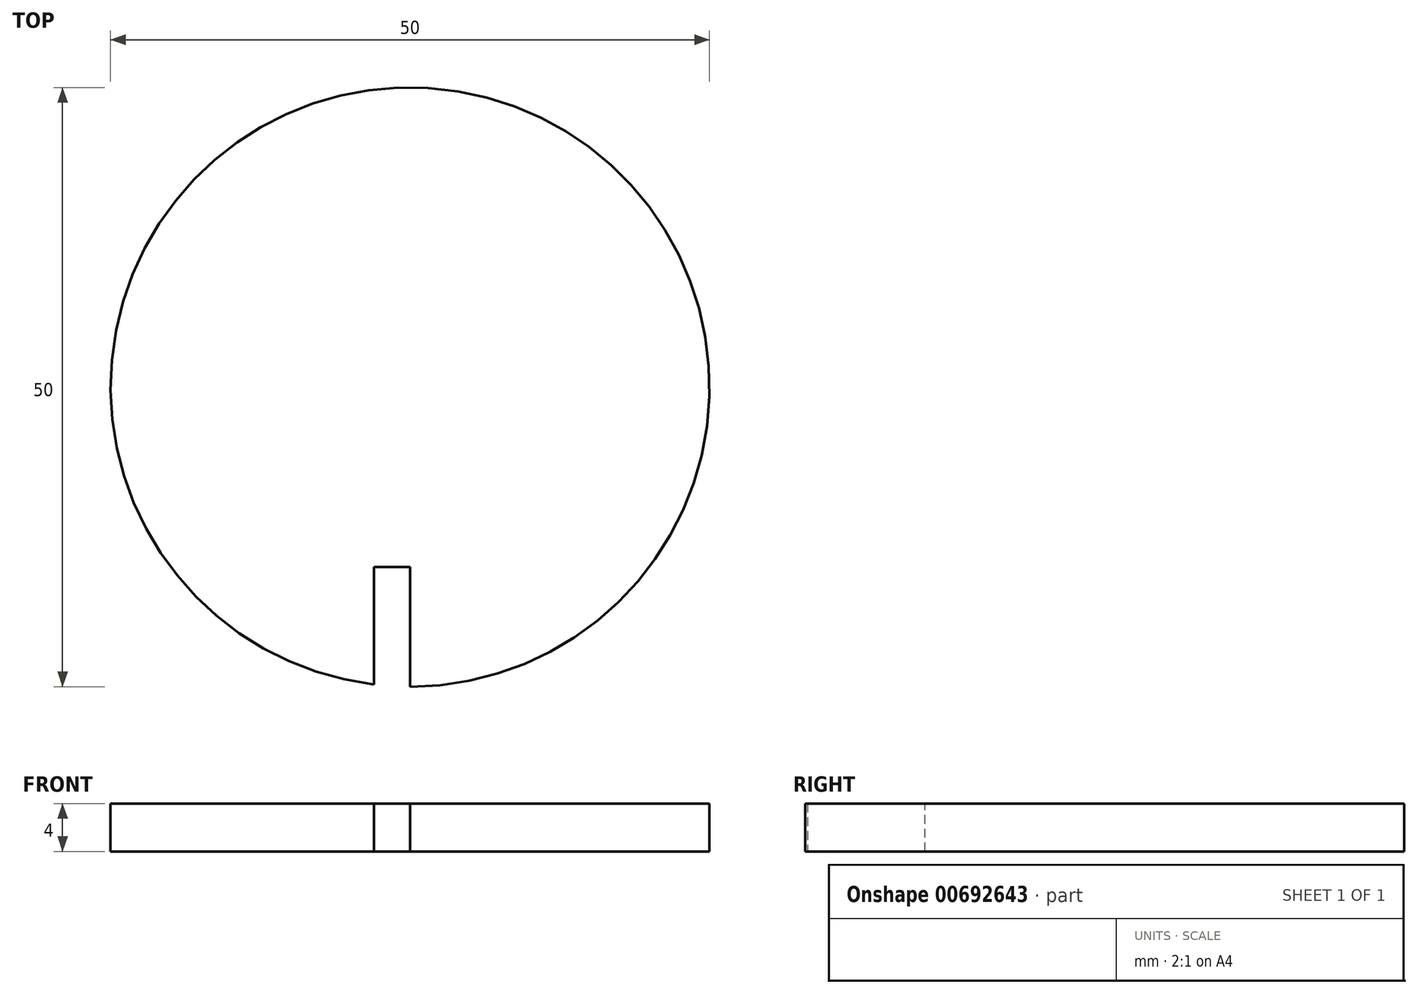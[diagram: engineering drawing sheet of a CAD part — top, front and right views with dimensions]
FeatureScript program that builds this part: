
annotation { "Feature Type Name" : "Feature", "Feature Type Description" : "" }
export const myFeature = defineFeature(function(context is Context, id is Id, definition is map)
    precondition{}
    {
        {
            var Q0;
            Q0=qCreatedBy(makeId("Top.planeOp"),FACE);
            var sketch = newSketch(context, id + "F0", { "sketchPlane" : qUnion([Q0])});
            skCircle(sketch, "E0", {"center": v(0, 0) * mm, "radius": 25 * mm});
            skSolve(sketch);
        }
        {
            var Q0;
            Q0 = qSketchRegion(id + "F0", true);
            extrude(context, id + "F1", {"entities" : qUnion([Q0]), "depth" : 4 * mm, "offsetDistance" : 25 * mm});
        }
        {
            var Q0;
            Q0=makeQuery(id+"F1.opExtrude","CAP_FACE",FACE,{"disambiguationData":[OSD([sQuery(id+"F0.wireOp",EDGE,"E0")])],"isStart":false});
            var sketch = newSketch(context, id + "F2", { "sketchPlane" : qUnion([Q0])});
            skLineSegment(sketch, "E1.bottom", {"start": v(0, -15) * mm, "end": v(-3, -15) * mm});
            skLineSegment(sketch, "E1.top", {"start": v(0, -25) * mm, "end": v(-3, -25) * mm});
            skLineSegment(sketch, "E1.left", {"start": v(0, -15) * mm, "end": v(0, -25) * mm});
            skLineSegment(sketch, "E1.right", {"start": v(-3, -15) * mm, "end": v(-3, -25) * mm});
            skSolve(sketch);
        }
        {
            var Q0;
            {var subQ0=sQuery(id+"F2.wireOp",EDGE,"E1.top");Q0=makeQuery(id+"F2.imprint","IMPRINT",FACE,{"disambiguationData":[TD([[makeQuery(id+"F2.imprint","IMPRINT",EDGE,{"derivedFrom":subQ0}),-1.0]])]});}
            var Q1;
            {var subQ0=sQuery(id+"F2.wireOp",EDGE,"E1.bottom");Q1=makeQuery(id+"F2.imprint","IMPRINT",FACE,{"disambiguationData":[TD([[makeQuery(id+"F2.imprint","IMPRINT",EDGE,{"derivedFrom":subQ0}),1.0]])]});}
            extrude(context, id + "F3", {"entities" : qUnion([Q0, Q1]), "operationType" : NewBodyOperationType.REMOVE, "endBound" : BoundingType.UP_TO_NEXT, "oppositeDirection" : true, "depth" : 25 * mm, "offsetDistance" : 25 * mm});
        }
    });
